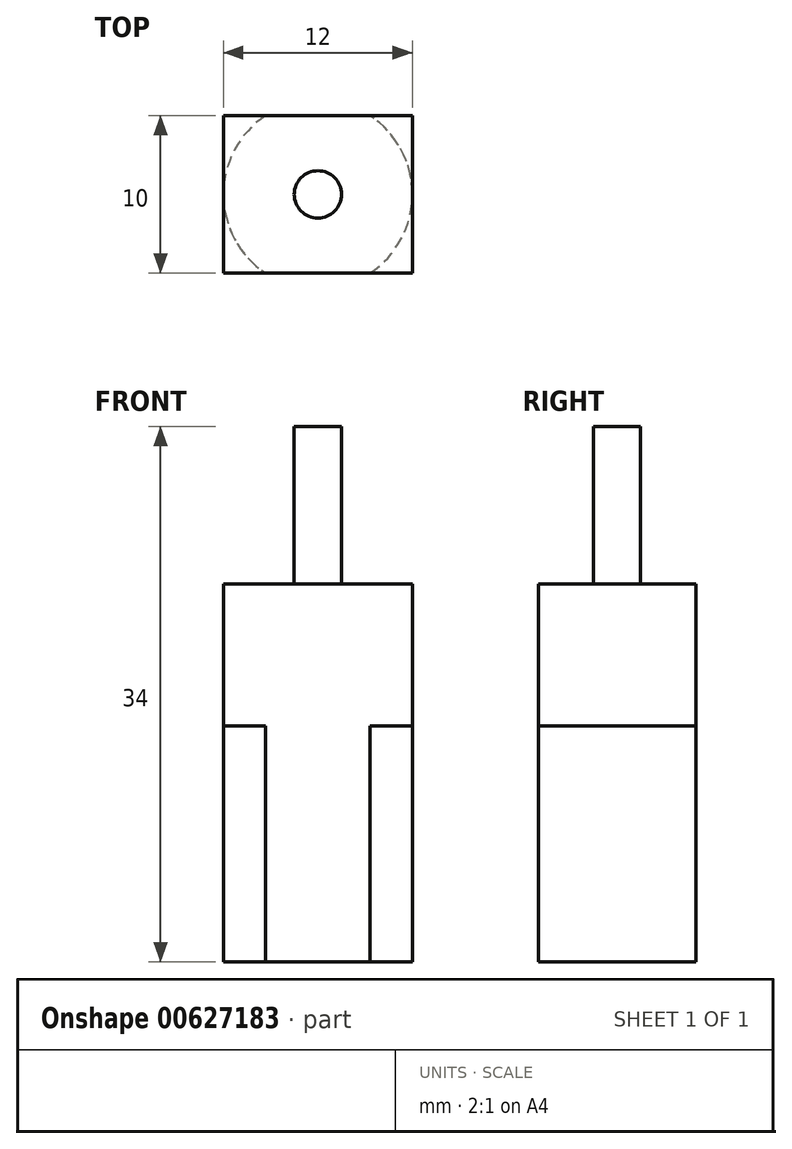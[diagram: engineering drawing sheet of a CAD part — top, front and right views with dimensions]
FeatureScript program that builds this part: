
annotation { "Feature Type Name" : "Feature", "Feature Type Description" : "" }
export const myFeature = defineFeature(function(context is Context, id is Id, definition is map)
    precondition{}
    {
        {
            var Q0;
            Q0=qCreatedBy(makeId("Top.planeOp"),FACE);
            var sketch = newSketch(context, id + "F0", { "sketchPlane" : qUnion([Q0])});
            skLineSegment(sketch, "E0", {"start": v(-3.32, 5) * mm, "end": v(3.32, 5) * mm});
            skLineSegment(sketch, "E1.MirrorCS", {"start": v(-3.32, -5) * mm, "end": v(3.32, -5) * mm});
            skArc(sketch, "E2", {"start": v(-3.32, 5) * mm, "mid": v(-6, 0) * mm, "end": v(-3.32, -5) * mm});
            skArc(sketch, "E3.MirrorCS", {"start": v(3.32, 5) * mm, "mid": v(6, 0) * mm, "end": v(3.32, -5) * mm});
            skSolve(sketch);
        }
        {
            var Q0;
            Q0 = qSketchRegion(id + "F0", true);
            extrude(context, id + "F1", {"entities" : qUnion([Q0]), "depth" : 15 * mm, "offsetDistance" : 25 * mm});
        }
        {
            var Q0;
            Q0=makeQuery(id+"F1.opExtrude","CAP_FACE",FACE,{"disambiguationData":[OSD([sQuery(id+"F0.wireOp",EDGE,"E0"),sQuery(id+"F0.wireOp",EDGE,"E1.MirrorCS"),sQuery(id+"F0.wireOp",EDGE,"E2"),sQuery(id+"F0.wireOp",EDGE,"E3.MirrorCS")])],"isStart":false});
            var sketch = newSketch(context, id + "F2", { "sketchPlane" : qUnion([Q0])});
            skLineSegment(sketch, "E4", {"start": v(-6, 5) * mm, "end": v(6, 5) * mm});
            skPoint(sketch, "E4.startSnap0", {"position": v(-6, 0) * mm});
            skPoint(sketch, "E4.endSnap0", {"position": v(6, 0) * mm});
            skLineSegment(sketch, "E5", {"start": v(6, 5) * mm, "end": v(6, -5) * mm});
            skLineSegment(sketch, "E6", {"start": v(6, -5) * mm, "end": v(-6, -5) * mm});
            skLineSegment(sketch, "E7", {"start": v(-6, -5) * mm, "end": v(-6, 5) * mm});
            skSolve(sketch);
        }
        {
            var Q0;
            Q0 = qSketchRegion(id + "F2", true);
            extrude(context, id + "F3", {"entities" : qUnion([Q0]), "operationType" : NewBodyOperationType.ADD, "depth" : 9 * mm, "offsetDistance" : 25 * mm});
        }
        {
            var Q0;
            Q0=makeQuery(id+"F3.opExtrude","CAP_FACE",FACE,{"disambiguationData":[OSD([sQuery(id+"F2.wireOp",EDGE,"E4"),sQuery(id+"F2.wireOp",EDGE,"E5"),sQuery(id+"F2.wireOp",EDGE,"E6"),sQuery(id+"F2.wireOp",EDGE,"E7")])],"isStart":false});
            var sketch = newSketch(context, id + "F4", { "sketchPlane" : qUnion([Q0])});
            skCircle(sketch, "E8", {"center": v(0, 0) * mm, "radius": 1.5 * mm});
            skSolve(sketch);
        }
        {
            var Q0;
            Q0 = qSketchRegion(id + "F4", true);
            extrude(context, id + "F5", {"entities" : qUnion([Q0]), "operationType" : NewBodyOperationType.ADD, "depth" : 10 * mm, "offsetDistance" : 25 * mm});
        }
    });
